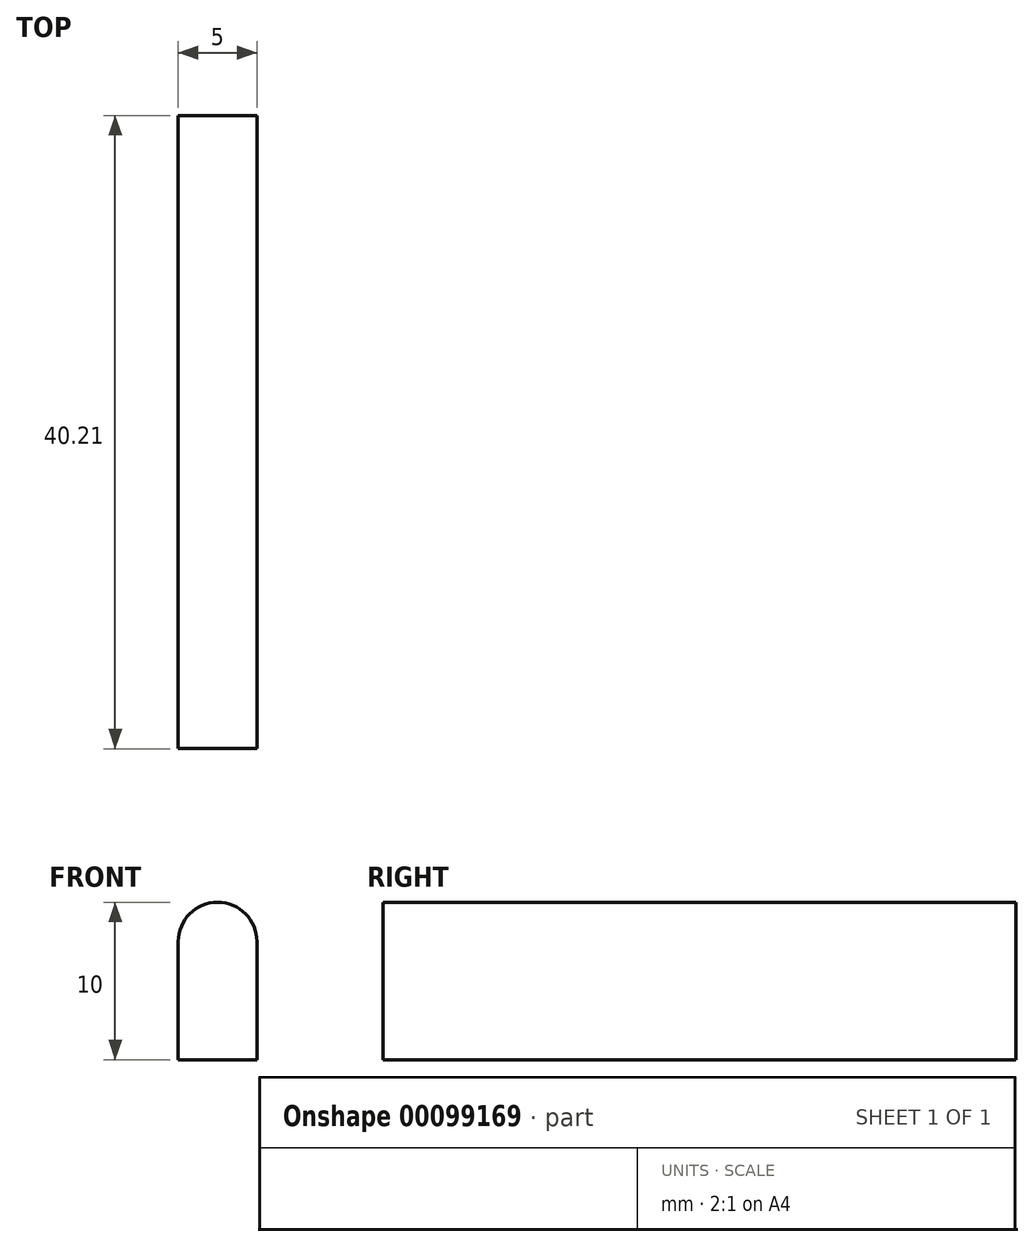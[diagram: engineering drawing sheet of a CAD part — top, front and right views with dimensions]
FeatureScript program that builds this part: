
annotation { "Feature Type Name" : "Feature", "Feature Type Description" : "" }
export const myFeature = defineFeature(function(context is Context, id is Id, definition is map)
    precondition{}
    {
        {
            var Q0;
            Q0=qCreatedBy(makeId("Top.planeOp"),FACE);
            var sketch = newSketch(context, id + "F0", { "sketchPlane" : qUnion([Q0])});
            skLineSegment(sketch, "E0", {"start": v(-44.69, -29.23) * mm, "end": v(-44.69, 25.77) * mm});
            skLineSegment(sketch, "E1", {"start": v(-44.69, 25.77) * mm, "end": v(35.31, 25.77) * mm});
            skLineSegment(sketch, "E2", {"start": v(35.31, 25.77) * mm, "end": v(35.31, -29.23) * mm});
            skLineSegment(sketch, "E3", {"start": v(35.31, -29.23) * mm, "end": v(30.31, -29.23) * mm});
            skLineSegment(sketch, "E4", {"start": v(30.31, -29.23) * mm, "end": v(30.31, 20.77) * mm});
            skLineSegment(sketch, "E5", {"start": v(30.31, 20.77) * mm, "end": v(-39.69, 20.77) * mm});
            skLineSegment(sketch, "E6", {"start": v(-39.69, 20.77) * mm, "end": v(-39.69, -29.23) * mm});
            skLineSegment(sketch, "E7", {"start": v(-39.69, -29.23) * mm, "end": v(-44.69, -29.23) * mm});
            skSolve(sketch);
        }
        {
            var Q0;
            Q0=makeQuery(id+"F0.imprint","IMPRINT",FACE,{"disambiguationData":[TD([[makeQuery(id+"F0.imprint","IMPRINT",EDGE,{"derivedFrom":sQuery(id+"F0.wireOp",EDGE,"E0")}),-1.0]])]});
            extrude(context, id + "F1", {"entities" : qUnion([Q0]), "depth" : 10 * mm});
        }
        {
            var Q0;
            Q0=makeQuery(id+"F1.opExtrude","CAP_EDGE",EDGE,{"disambiguationData":[OSD([sQuery(id+"F0.wireOp",EDGE,"E0")])],"isStart":false});
            var Q1;
            Q1=makeQuery(id+"F1.opExtrude","CAP_EDGE",EDGE,{"disambiguationData":[OSD([sQuery(id+"F0.wireOp",EDGE,"E6")])],"isStart":false});
            var Q2;
            Q2=makeQuery(id+"F1.opExtrude","CAP_EDGE",EDGE,{"disambiguationData":[OSD([sQuery(id+"F0.wireOp",EDGE,"E4")])],"isStart":false});
            var Q3;
            Q3=makeQuery(id+"F1.opExtrude","CAP_EDGE",EDGE,{"disambiguationData":[OSD([sQuery(id+"F0.wireOp",EDGE,"E2")])],"isStart":false});
            fillet(context, id + "F2", {"entities" : qUnion([Q0, Q1, Q2, Q3]), "radius" : 2.5 * mm, "tangentPropagation" : true, "allowEdgeOverflow" : false});
        }
        {
            var Q0;
            Q0=qCreatedBy(makeId("Top.planeOp"),FACE);
            var sketch = newSketch(context, id + "F3", { "sketchPlane" : qUnion([Q0])});
            skLineSegment(sketch, "E8.bottom", {"start": v(-35.5, 40) * mm, "end": v(47.26, 40) * mm});
            skLineSegment(sketch, "E8.top", {"start": v(-35.5, -43.54) * mm, "end": v(47.26, -43.54) * mm});
            skLineSegment(sketch, "E8.left", {"start": v(-35.5, 40) * mm, "end": v(-35.5, -43.54) * mm});
            skLineSegment(sketch, "E8.right", {"start": v(47.26, 40) * mm, "end": v(47.26, -43.54) * mm});
            skLineSegment(sketch, "E9.bottom", {"start": v(-54.72, 10.98) * mm, "end": v(-24.12, 10.98) * mm});
            skLineSegment(sketch, "E9.top", {"start": v(-54.72, 54.52) * mm, "end": v(-24.12, 54.52) * mm});
            skLineSegment(sketch, "E9.left", {"start": v(-54.72, 10.98) * mm, "end": v(-54.72, 54.52) * mm});
            skLineSegment(sketch, "E9.right", {"start": v(-24.12, 10.98) * mm, "end": v(-24.12, 54.52) * mm});
            skLineSegment(sketch, "E10.bottom", {"start": v(-54.72, 10.98) * mm, "end": v(-54.72, 10.98) * mm});
            skLineSegment(sketch, "E10.top", {"start": v(-54.72, -10.2) * mm, "end": v(-54.72, -10.2) * mm});
            skLineSegment(sketch, "E10.left", {"start": v(-54.72, 10.98) * mm, "end": v(-54.72, -10.2) * mm});
            skLineSegment(sketch, "E10.right", {"start": v(-54.72, 10.98) * mm, "end": v(-54.72, -10.2) * mm});
            skLineSegment(sketch, "E11.bottom", {"start": v(-54.72, -10.2) * mm, "end": v(-24.12, -10.2) * mm});
            skLineSegment(sketch, "E11.left", {"start": v(-54.72, -10.2) * mm, "end": v(-54.72, 10.98) * mm});
            skLineSegment(sketch, "E11.right", {"start": v(-24.12, -10.2) * mm, "end": v(-24.12, 10.98) * mm});
            skSolve(sketch);
        }
        {
            var Q0;
            {var subQ2=sQuery(id+"F3.wireOp",EDGE,"E8.top");Q0=makeQuery(id+"F3.imprint","IMPRINT",FACE,{"disambiguationData":[TD([[makeQuery(id+"F3.imprint","IMPRINT",EDGE,{"derivedFrom":subQ2}),1.0]])]});}
            var Q1;
            {var subQ0=sQuery(id+"F3.wireOp",EDGE,"E9.top");Q1=makeQuery(id+"F3.imprint","IMPRINT",FACE,{"disambiguationData":[TD([[makeQuery(id+"F3.imprint","IMPRINT",EDGE,{"derivedFrom":subQ0}),-1.0]])]});}
            var Q2;
            {var subQ5=sQuery(id+"F3.wireOp",EDGE,"E11.right");Q2=makeQuery(id+"F3.imprint","IMPRINT",FACE,{"disambiguationData":[TD([[makeQuery(id+"F3.imprint","IMPRINT",EDGE,{"derivedFrom":subQ5}),1.0]])]});}
            extrude(context, id + "F4", {"entities" : qUnion([Q0, Q1, Q2]), "operationType" : NewBodyOperationType.REMOVE, "depth" : 25 * mm});
        }
        {
            var Q0;
            {var subQ0=sQuery(id+"F3.wireOp",EDGE,"E9.right");Q0=makeQuery(id+"F4.boolean.opBoolean","COPY",FACE,{"derivedFrom":makeQuery(id+"F4.opExtrude","SWEPT_FACE",FACE,{"disambiguationData":[OSD([subQ0]),TDD([makeQuery(id+"F3.imprint","IMPRINT",EDGE,{"disambiguationData":[TD([[makeQuery(id+"F3.imprint","INTERSECT",VERTEX,{"derivedFrom":[sQuery(id+"F3.wireOp",EDGE,"E8.bottom"),subQ0]}),1.0]])],"derivedFrom":subQ0})])]})});}
            extrude(context, id + "F5", {"entities" : qUnion([Q0]), "operationType" : NewBodyOperationType.REMOVE, "oppositeDirection" : true, "depth" : 25 * mm});
        }
    });
